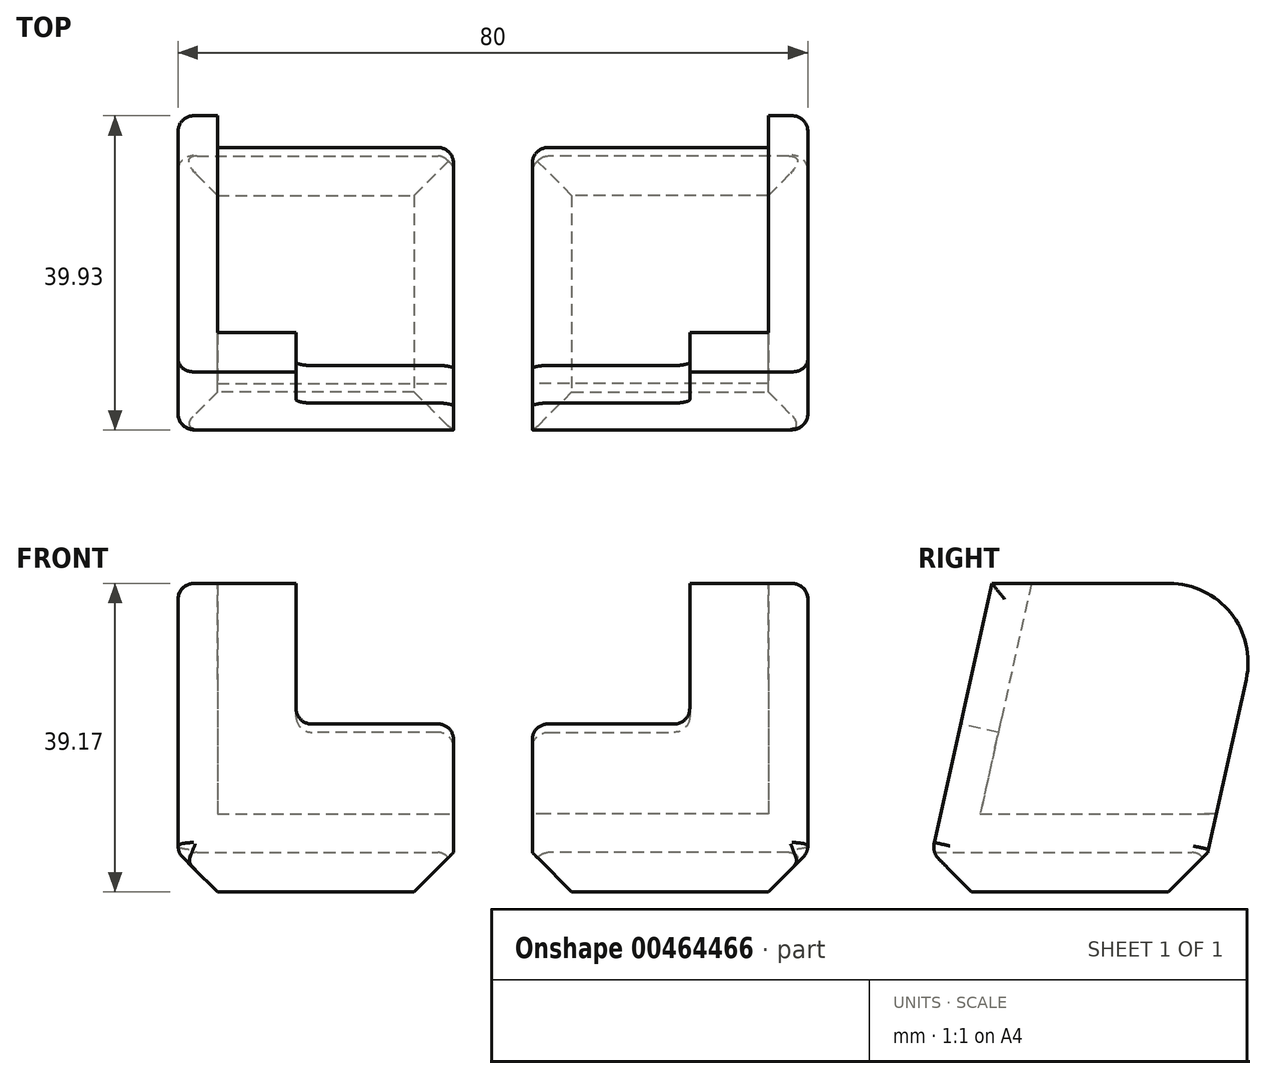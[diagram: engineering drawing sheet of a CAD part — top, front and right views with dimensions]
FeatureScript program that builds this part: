
annotation { "Feature Type Name" : "Feature", "Feature Type Description" : "" }
export const myFeature = defineFeature(function(context is Context, id is Id, definition is map)
    precondition{}
    {
        {
            var Q0;
            Q0=qCreatedBy(makeId("Right.planeOp"),FACE);
            var sketch = newSketch(context, id + "F0", { "sketchPlane" : qUnion([Q0])});
            skLineSegment(sketch, "E0", {"start": v(0, 0) * mm, "end": v(7.58, 34.17) * mm});
            skLineSegment(sketch, "E1", {"start": v(7.58, 34.17) * mm, "end": v(42.58, 34.17) * mm});
            skLineSegment(sketch, "E2", {"start": v(42.58, 34.17) * mm, "end": v(35, 0) * mm});
            skLineSegment(sketch, "E3", {"start": v(35, 0) * mm, "end": v(0, 0) * mm});
            skSolve(sketch);
        }
        {
            var Q0;
            Q0=makeQuery(id+"F0.imprint","IMPRINT",FACE,{"disambiguationData":[TD([[makeQuery(id+"F0.imprint","IMPRINT",EDGE,{"derivedFrom":sQuery(id+"F0.wireOp",EDGE,"E0")}),-1.0]])]});
            extrude(context, id + "F1", {"entities" : qUnion([Q0]), "oppositeDirection" : true, "depth" : 35 * mm});
        }
        {
            var Q0;
            Q0=makeQuery(id+"F1.opExtrude","CAP_FACE",FACE,{"disambiguationData":[OSD([sQuery(id+"F0.wireOp",EDGE,"E0"),sQuery(id+"F0.wireOp",EDGE,"E1"),sQuery(id+"F0.wireOp",EDGE,"E2"),sQuery(id+"F0.wireOp",EDGE,"E3")])],"isStart":true});
            var sketch = newSketch(context, id + "F2", { "sketchPlane" : qUnion([Q0])});
            skLineSegment(sketch, "E4", {"start": v(12.58, 34.17) * mm, "end": v(6.08, 4.88) * mm});
            skLineSegment(sketch, "E5", {"start": v(6.08, 4.88) * mm, "end": v(36.08, 4.88) * mm});
            skLineSegment(sketch, "E6", {"start": v(36.08, 4.88) * mm, "end": v(42.58, 34.17) * mm});
            skLineSegment(sketch, "E7", {"start": v(42.58, 34.17) * mm, "end": v(12.58, 34.17) * mm});
            skSolve(sketch);
        }
        {
            var Q0;
            Q0=makeQuery(id+"F2.imprint","IMPRINT",FACE,{"disambiguationData":[TD([[makeQuery(id+"F2.imprint","IMPRINT",EDGE,{"derivedFrom":sQuery(id+"F2.wireOp",EDGE,"E4")}),1.0]])]});
            extrude(context, id + "F3", {"entities" : qUnion([Q0]), "operationType" : NewBodyOperationType.REMOVE, "oppositeDirection" : true, "depth" : 30 * mm});
        }
        {
            var Q0;
            Q0=makeQuery(id+"F1.opExtrude","SWEPT_FACE",FACE,{"disambiguationData":[OSD([sQuery(id+"F0.wireOp",EDGE,"E0")])]});
            var sketch = newSketch(context, id + "F4", { "sketchPlane" : qUnion([Q0])});
            skLineSegment(sketch, "E8.bottom", {"start": v(0, 35) * mm, "end": v(-20, 35) * mm});
            skLineSegment(sketch, "E8.top", {"start": v(0, 16.72) * mm, "end": v(-20, 16.72) * mm});
            skLineSegment(sketch, "E8.left", {"start": v(0, 35) * mm, "end": v(0, 16.72) * mm});
            skLineSegment(sketch, "E8.right", {"start": v(-20, 35) * mm, "end": v(-20, 16.72) * mm});
            skSolve(sketch);
        }
        {
            var Q0;
            Q0=makeQuery(id+"F4.imprint","IMPRINT",FACE,{"disambiguationData":[TD([[makeQuery(id+"F4.imprint","IMPRINT",EDGE,{"derivedFrom":sQuery(id+"F4.wireOp",EDGE,"E8.bottom")}),-1.0]])]});
            extrude(context, id + "F5", {"entities" : qUnion([Q0]), "operationType" : NewBodyOperationType.REMOVE, "endBound" : BoundingType.THROUGH_ALL, "oppositeDirection" : true, "depth" : 25 * mm});
        }
        {
            var Q0;
            Q0=makeQuery(id+"F1.opExtrude","SWEPT_FACE",FACE,{"disambiguationData":[OSD([sQuery(id+"F0.wireOp",EDGE,"E1")])]});
            var sketch = newSketch(context, id + "F6", { "sketchPlane" : qUnion([Q0])});
            skLineSegment(sketch, "E9", {"start": v(-20, 7.58) * mm, "end": v(-20, 12.58) * mm});
            skSolve(sketch);
        }
        {
            var Q0;
            {var subQ0=sQuery(id+"F6.wireOp",EDGE,"E9");Q0=makeQuery(id+"F6.imprint","IMPRINT",FACE,{"disambiguationData":[TD([[makeQuery(id+"F6.imprint","IMPRINT",EDGE,{"derivedFrom":subQ0}),-1.0]])]});}
            extrude(context, id + "F7", {"entities" : qUnion([Q0]), "operationType" : NewBodyOperationType.REMOVE, "oppositeDirection" : true, "depth" : 5 * mm});
        }
        {
            var Q0;
            Q0=makeQuery(id+"F1.opExtrude","SWEPT_FACE",FACE,{"disambiguationData":[OSD([sQuery(id+"F0.wireOp",EDGE,"E3")])]});
            extrude(context, id + "F8", {"entities" : qUnion([Q0]), "operationType" : NewBodyOperationType.ADD, "depth" : 5 * mm});
        }
        {
            var Q0;
            Q0=makeQuery(id+"F8.opExtrude","CAP_FACE",FACE,{"disambiguationData":[OSD([sQuery(id+"F0.wireOp",EDGE,"E3")])],"isStart":false});
            chamfer(context, id + "F9", {"entities" : qUnion([Q0]), "width" : 5 * mm, "tangentPropagation" : true});
        }
        {
            var Q0;
            Q0=makeQuery(id+"F1.opExtrude","CAP_EDGE",EDGE,{"disambiguationData":[OSD([sQuery(id+"F0.wireOp",EDGE,"E1")])],"isStart":false});
            var Q1;
            Q1=makeQuery(id+"F7.boolean.opBoolean","COPY",EDGE,{"derivedFrom":makeQuery(id+"F7.opExtrude","CAP_EDGE",EDGE,{"disambiguationData":[OSD([sQuery(id+"F6.wireOp",EDGE,"E9")])],"isStart":true})});
            var Q2;
            Q2=makeQuery(id+"F5.boolean.opBoolean","COPY",EDGE,{"derivedFrom":makeQuery(id+"F5.opExtrude","SWEPT_EDGE",EDGE,{"disambiguationData":[OSD([sQuery(id+"F4.wireOp",EDGE,"E8.top"),sQuery(id+"F4.wireOp",EDGE,"E8.right")])]})});
            var Q3;
            Q3=makeQuery(id+"F5.boolean.opBoolean","COPY",EDGE,{"derivedFrom":makeQuery(id+"F5.opExtrude","SWEPT_EDGE",EDGE,{"disambiguationData":[OSD([sQuery(id+"F0.wireOp",EDGE,"E0"),sQuery(id+"F4.wireOp",EDGE,"E8.top"),sQuery(id+"F4.wireOp",EDGE,"E8.left")])]})});
            var Q4;
            Q4=makeQuery(id+"F1.opExtrude","CAP_EDGE",EDGE,{"disambiguationData":[OSD([sQuery(id+"F0.wireOp",EDGE,"E0")])],"isStart":false});
            var Q5;
            Q5=makeQuery(id+"F1.opExtrude","CAP_EDGE",EDGE,{"disambiguationData":[OSD([sQuery(id+"F0.wireOp",EDGE,"E2")])],"isStart":false});
            var Q6;
            {var subQ0=sQuery(id+"F0.wireOp",EDGE,"E0");Q6=makeQuery(id+"F9.opChamfer","BLEND_EDGE",EDGE,{"blendedFrom":[makeQuery(id+"F8.opExtrude","CAP_EDGE",EDGE,{"disambiguationData":[OSD([subQ0,sQuery(id+"F0.wireOp",EDGE,"E3")])],"isStart":false}),makeQuery(id+"F1.opExtrude","SWEPT_FACE",FACE,{"disambiguationData":[OSD([subQ0])]})],"blendedInto":[makeQuery(id+"F1.opExtrude","SWEPT_FACE",FACE,{"disambiguationData":[OSD([subQ0])]})]});}
            fillet(context, id + "F10", {"entities" : qUnion([Q0, Q1, Q2, Q3, Q4, Q5, Q6]), "radius" : 2 * mm, "tangentPropagation" : true, "allowEdgeOverflow" : false});
        }
        {
            var Q0;
            Q0=makeQuery(id+"F1.opExtrude","CAP_EDGE",EDGE,{"disambiguationData":[OSD([sQuery(id+"F0.wireOp",EDGE,"E2")])],"isStart":true});
            fillet(context, id + "F11", {"entities" : qUnion([Q0]), "radius" : 2 * mm, "tangentPropagation" : true, "allowEdgeOverflow" : false});
        }
        {
            var Q0;
            {var subQ0=sQuery(id+"F0.wireOp",EDGE,"E3");var subQ1=makeQuery(id+"F1.opExtrude","CAP_EDGE",EDGE,{"disambiguationData":[OSD([subQ0])],"isStart":false});Q0=makeQuery(id+"F9.opChamfer","BLEND_EDGE",EDGE,{"blendedFrom":[makeQuery(id+"F8.opExtrude","CAP_EDGE",EDGE,{"disambiguationData":[OSD([subQ0]),TDD([subQ1])],"isStart":false}),makeQuery(id+"F8.boolean.opBoolean","MERGE",FACE,{"derivedFrom":[makeQuery(id+"F1.opExtrude","CAP_FACE",FACE,{"disambiguationData":[OSD([sQuery(id+"F0.wireOp",EDGE,"E0"),sQuery(id+"F0.wireOp",EDGE,"E1"),sQuery(id+"F0.wireOp",EDGE,"E2"),subQ0])],"isStart":false}),makeQuery(id+"F8.opExtrude","SWEPT_FACE",FACE,{"disambiguationData":[OSD([subQ0]),TDD([subQ1])]})]})],"blendedInto":[makeQuery(id+"F8.boolean.opBoolean","MERGE",FACE,{"derivedFrom":[makeQuery(id+"F1.opExtrude","CAP_FACE",FACE,{"disambiguationData":[OSD([sQuery(id+"F0.wireOp",EDGE,"E0"),sQuery(id+"F0.wireOp",EDGE,"E1"),sQuery(id+"F0.wireOp",EDGE,"E2"),subQ0])],"isStart":false}),makeQuery(id+"F8.opExtrude","SWEPT_FACE",FACE,{"disambiguationData":[OSD([subQ0]),TDD([subQ1])]})]})]});}
            fillet(context, id + "F12", {"entities" : qUnion([Q0]), "radius" : 2 * mm, "tangentPropagation" : true, "allowEdgeOverflow" : false});
        }
        {
            var Q0;
            Q0=makeQuery(id+"F1.opExtrude","SWEPT_EDGE",EDGE,{"disambiguationData":[OSD([sQuery(id+"F0.wireOp",EDGE,"E1"),sQuery(id+"F0.wireOp",EDGE,"E2")])]});
            fillet(context, id + "F13", {"entities" : qUnion([Q0]), "radius" : 10 * mm, "tangentPropagation" : true, "allowEdgeOverflow" : false});
        }
        {
            var Q0;
            Q0=qCreatedBy(makeId("Right.planeOp"),FACE);
            cPlane(context, id + "F14", {"entities" : qUnion([Q0]), "cplaneType" : CPlaneType.OFFSET, "offset" : 5 * mm, "width" : 150 * mm, "height" : 150 * mm});
        }
        {
            var Q0;
            Q0=makeQuery(id+"F1.opExtrude","SWEPT_BODY",BODY,{"disambiguationData":[OSD([sQuery(id+"F0.wireOp",EDGE,"E0"),sQuery(id+"F0.wireOp",EDGE,"E1"),sQuery(id+"F0.wireOp",EDGE,"E2"),sQuery(id+"F0.wireOp",EDGE,"E3")])]});
            var Q1;
            Q1=qCreatedBy(id+"F14.planeOp",FACE);
            mirror(context, id + "F15", {"entities" : qUnion([Q0]), "mirrorPlane" : qUnion([Q1])});
        }
    });
